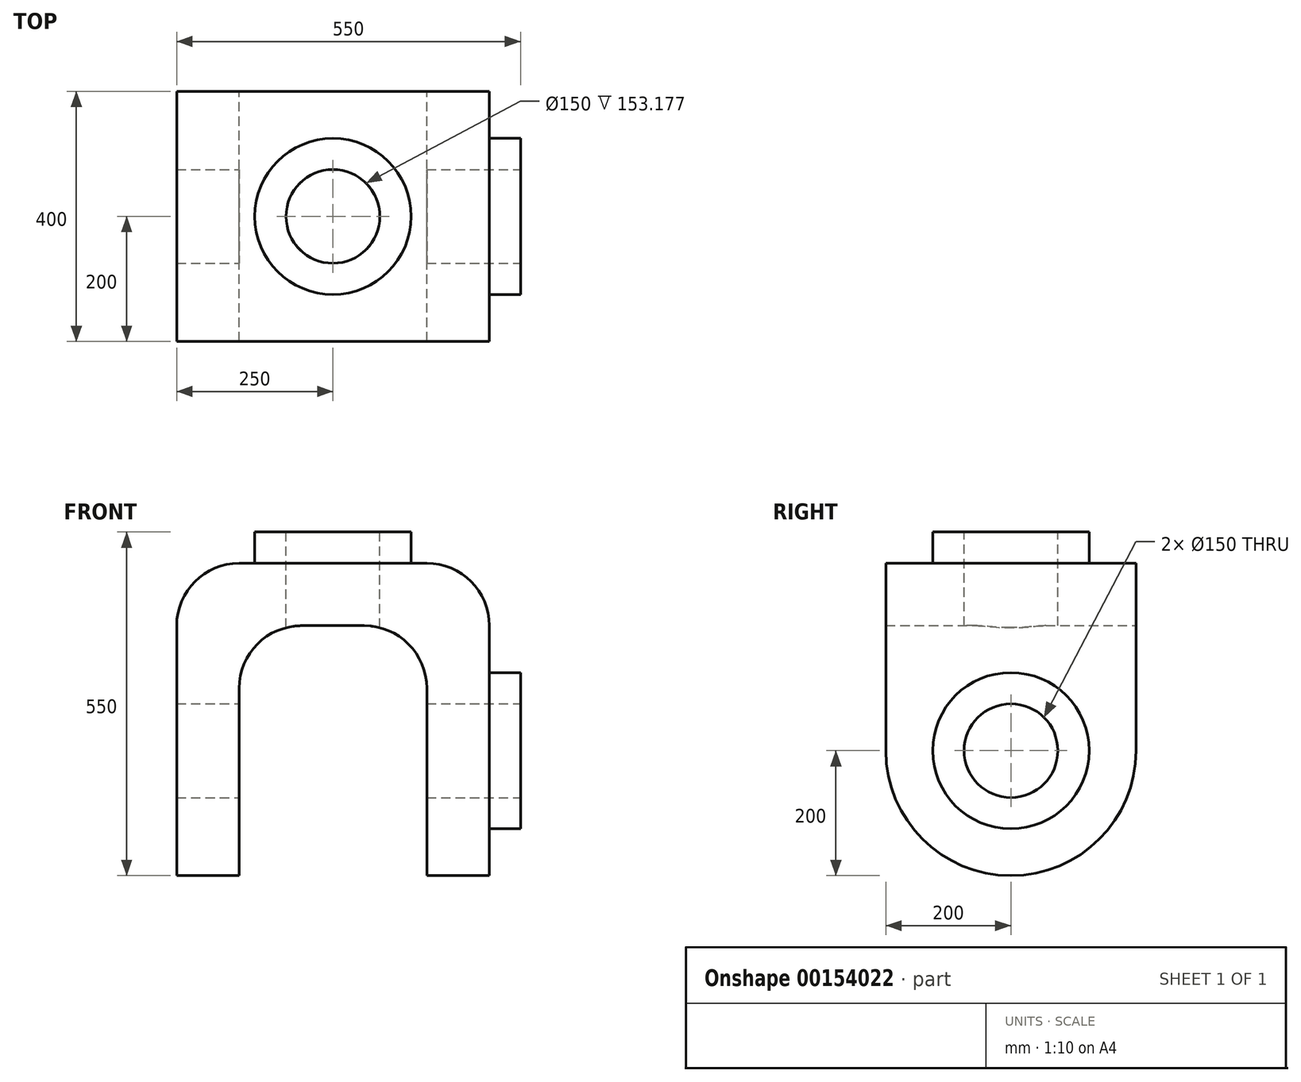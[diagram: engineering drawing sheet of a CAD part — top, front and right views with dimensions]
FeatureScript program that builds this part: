
annotation { "Feature Type Name" : "Feature", "Feature Type Description" : "" }
export const myFeature = defineFeature(function(context is Context, id is Id, definition is map)
    precondition{}
    {
        {
            var Q0;
            Q0=qCreatedBy(makeId("Front.planeOp"),FACE);
            var sketch = newSketch(context, id + "F0", { "sketchPlane" : qUnion([Q0])});
            skLineSegment(sketch, "E0.bottom", {"start": v(150, 250) * mm, "end": v(-150, 250) * mm});
            skLineSegment(sketch, "E0.top", {"start": v(250, -250) * mm, "end": v(150, -250) * mm});
            skLineSegment(sketch, "E0.left", {"start": v(250, 150) * mm, "end": v(250, -250) * mm});
            skLineSegment(sketch, "E0.right", {"start": v(-250, 150) * mm, "end": v(-250, -250) * mm});
            skPoint(sketch, "E0.middle", {"position": v(0, 0) * mm});
            skLineSegment(sketch, "E1.0", {"start": v(150, 50) * mm, "end": v(150, -250) * mm});
            skLineSegment(sketch, "E2.0", {"start": v(50, 150) * mm, "end": v(-50, 150) * mm});
            skLineSegment(sketch, "E3.0", {"start": v(-150, 50) * mm, "end": v(-150, -250) * mm});
            skLineSegment(sketch, "E4.trimOffspring", {"start": v(-150, -250) * mm, "end": v(-250, -250) * mm});
            skPoint(sketch, "E5.visualSharp", {"position": v(-250, 250) * mm});
            skArc(sketch, "E5.filletArc", {"start": v(-150, 250) * mm, "mid": v(-220.71, 220.71) * mm, "end": v(-250, 150) * mm});
            skArc(sketch, "E6.filletArc", {"start": v(-50, 150) * mm, "mid": v(-120.71, 120.71) * mm, "end": v(-150, 50) * mm});
            skPoint(sketch, "E7.visualSharp", {"position": v(150, 150) * mm});
            skArc(sketch, "E7.filletArc", {"start": v(150, 50) * mm, "mid": v(120.71, 120.71) * mm, "end": v(50, 150) * mm});
            skPoint(sketch, "E8.visualSharp", {"position": v(250, 250) * mm});
            skArc(sketch, "E8.filletArc", {"start": v(250, 150) * mm, "mid": v(220.71, 220.71) * mm, "end": v(150, 250) * mm});
            skSolve(sketch);
        }
        {
            var Q0;
            Q0=makeQuery(id+"F0.imprint","IMPRINT",FACE,{"disambiguationData":[TD([[makeQuery(id+"F0.imprint","IMPRINT",EDGE,{"derivedFrom":sQuery(id+"F0.wireOp",EDGE,"E0.bottom")}),1.0]])]});
            extrude(context, id + "F1", {"entities" : qUnion([Q0]), "depth" : 400 * mm, "symmetric" : true});
        }
        {
            var Q0;
            Q0=makeQuery(id+"F1.opExtrude","CAP_EDGE",EDGE,{"disambiguationData":[OSD([sQuery(id+"F0.wireOp",EDGE,"E4.trimOffspring")])],"isStart":false});
            var Q1;
            Q1=makeQuery(id+"F1.opExtrude","CAP_EDGE",EDGE,{"disambiguationData":[OSD([sQuery(id+"F0.wireOp",EDGE,"E4.trimOffspring")])],"isStart":true});
            var Q2;
            Q2=makeQuery(id+"F1.opExtrude","CAP_EDGE",EDGE,{"disambiguationData":[OSD([sQuery(id+"F0.wireOp",EDGE,"E0.top")])],"isStart":false});
            var Q3;
            Q3=makeQuery(id+"F1.opExtrude","CAP_EDGE",EDGE,{"disambiguationData":[OSD([sQuery(id+"F0.wireOp",EDGE,"E0.top")])],"isStart":true});
            fillet(context, id + "F2", {"entities" : qUnion([Q0, Q1, Q2, Q3]), "radius" : 200 * mm, "tangentPropagation" : true, "allowEdgeOverflow" : false});
        }
        {
            var Q0;
            Q0=makeQuery(id+"F1.opExtrude","SWEPT_FACE",FACE,{"disambiguationData":[OSD([sQuery(id+"F0.wireOp",EDGE,"E0.left")])]});
            var sketch = newSketch(context, id + "F3", { "sketchPlane" : qUnion([Q0])});
            skLineSegment(sketch, "E9", {"start": v(-200, -50) * mm, "end": v(200, -50) * mm, "construction": true});
            skCircle(sketch, "E10", {"center": v(0, -50) * mm, "radius": 125 * mm});
            skSolve(sketch);
        }
        {
            var Q0;
            Q0=makeQuery(id+"F3.imprint","IMPRINT",FACE,{"disambiguationData":[TD([[makeQuery(id+"F3.imprint","IMPRINT",EDGE,{"derivedFrom":sQuery(id+"F3.wireOp",EDGE,"E10")}),1.0]])]});
            extrude(context, id + "F4", {"entities" : qUnion([Q0]), "operationType" : NewBodyOperationType.ADD, "depth" : 50 * mm});
        }
        {
            var Q0;
            Q0=makeQuery(id+"F1.opExtrude","SWEPT_FACE",FACE,{"disambiguationData":[OSD([sQuery(id+"F0.wireOp",EDGE,"E0.bottom")])]});
            var sketch = newSketch(context, id + "F5", { "sketchPlane" : qUnion([Q0])});
            skCircle(sketch, "E11", {"center": v(0, 0) * mm, "radius": 125 * mm});
            skSolve(sketch);
        }
        {
            var Q0;
            Q0=makeQuery(id+"F5.imprint","IMPRINT",FACE,{"disambiguationData":[TD([[makeQuery(id+"F5.imprint","IMPRINT",EDGE,{"derivedFrom":sQuery(id+"F5.wireOp",EDGE,"E11")}),1.0]])]});
            extrude(context, id + "F6", {"entities" : qUnion([Q0]), "operationType" : NewBodyOperationType.ADD, "depth" : 50 * mm});
        }
        {
            var Q0;
            Q0=qCreatedBy(makeId("Right.planeOp"),FACE);
            var sketch = newSketch(context, id + "F7", { "sketchPlane" : qUnion([Q0])});
            skCircle(sketch, "E12.0", {"center": v(0, -50) * mm, "radius": 125 * mm, "construction": true});
            skCircle(sketch, "E13", {"center": v(0, -50) * mm, "radius": 75 * mm});
            skSolve(sketch);
        }
        {
            var Q0;
            Q0=makeQuery(id+"F7.imprint","IMPRINT",FACE,{"disambiguationData":[TD([[makeQuery(id+"F7.imprint","IMPRINT",EDGE,{"derivedFrom":sQuery(id+"F7.wireOp",EDGE,"E13")}),1.0]])]});
            var Q1;
            Q1=sQuery(id+"F7.wireOp",EDGE,"E13");
            extrude(context, id + "F8", {"entities" : qUnion([Q0]), "operationType" : NewBodyOperationType.REMOVE, "surfaceEntities" : qUnion([Q1]), "oppositeDirection" : true, "depth" : 700 * mm, "symmetric" : true});
        }
        {
            var Q0;
            Q0=makeQuery(id+"F6.opExtrude","CAP_FACE",FACE,{"disambiguationData":[OSD([sQuery(id+"F5.wireOp",EDGE,"E11")])],"isStart":false});
            var sketch = newSketch(context, id + "F9", { "sketchPlane" : qUnion([Q0])});
            skCircle(sketch, "E14", {"center": v(0, 0) * mm, "radius": 75 * mm});
            skSolve(sketch);
        }
        {
            var Q0;
            Q0=makeQuery(id+"F9.imprint","IMPRINT",FACE,{"disambiguationData":[TD([[makeQuery(id+"F9.imprint","IMPRINT",EDGE,{"derivedFrom":sQuery(id+"F9.wireOp",EDGE,"E14")}),1.0]])]});
            var Q1;
            Q1=sQuery(id+"F9.wireOp",EDGE,"E14");
            extrude(context, id + "F10", {"entities" : qUnion([Q0]), "operationType" : NewBodyOperationType.REMOVE, "surfaceEntities" : qUnion([Q1]), "oppositeDirection" : true, "depth" : 312.5 * mm});
        }
    });
